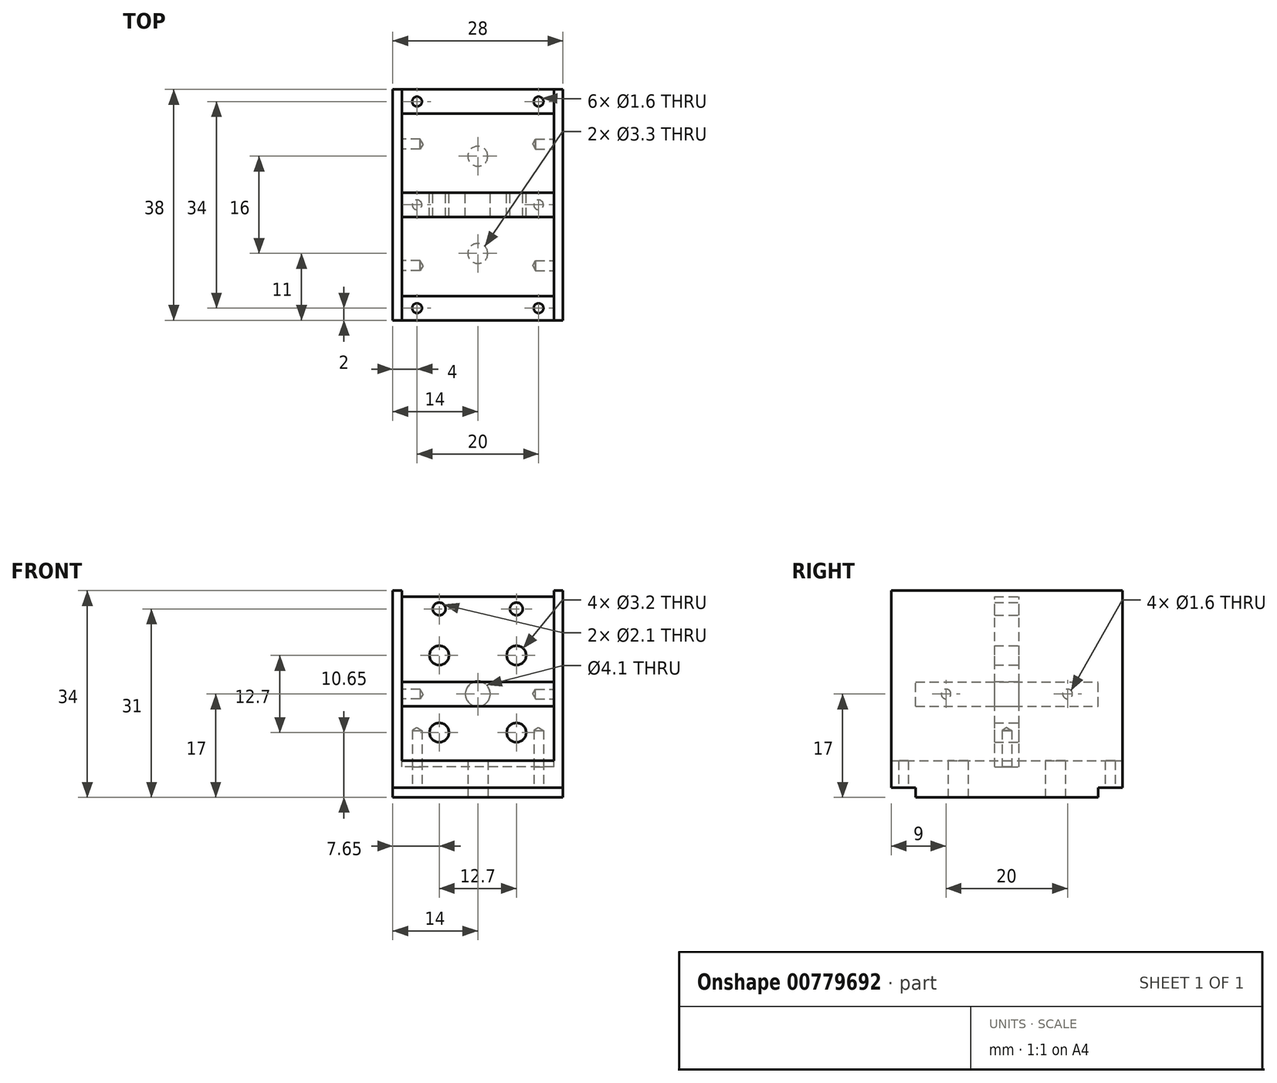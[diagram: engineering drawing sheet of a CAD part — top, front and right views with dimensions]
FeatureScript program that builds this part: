
annotation { "Feature Type Name" : "Feature", "Feature Type Description" : "" }
export const myFeature = defineFeature(function(context is Context, id is Id, definition is map)
    precondition{}
    {
        {
            var Q0;
            Q0=qCreatedBy(makeId("Front.planeOp"),FACE);
            var sketch = newSketch(context, id + "F0", { "sketchPlane" : qUnion([Q0])});
            skLineSegment(sketch, "E0.bottom", {"start": v(14, -17) * mm, "end": v(-14, -17) * mm});
            skLineSegment(sketch, "E0.top", {"start": v(14, 17) * mm, "end": v(12.5, 17) * mm});
            skLineSegment(sketch, "E0.left", {"start": v(14, -17) * mm, "end": v(14, 17) * mm});
            skLineSegment(sketch, "E0.right", {"start": v(-14, -17) * mm, "end": v(-14, 17) * mm});
            skPoint(sketch, "E0.middle", {"position": v(0, 0) * mm});
            skLineSegment(sketch, "E1.bottom", {"start": v(12.5, -11) * mm, "end": v(-12.5, -11) * mm});
            skLineSegment(sketch, "E1.left", {"start": v(12.5, -11) * mm, "end": v(12.5, 17) * mm});
            skLineSegment(sketch, "E1.right", {"start": v(-12.5, -11) * mm, "end": v(-12.5, 17) * mm});
            skLineSegment(sketch, "E2.trimOffspring", {"start": v(-12.5, 17) * mm, "end": v(-14, 17) * mm});
            skSolve(sketch);
        }
        {
            var Q0;
            Q0=makeQuery(id+"F0.imprint","IMPRINT",FACE,{"disambiguationData":[TD([[makeQuery(id+"F0.imprint","IMPRINT",EDGE,{"derivedFrom":sQuery(id+"F0.wireOp",EDGE,"E0.bottom")}),-1.0]])]});
            extrude(context, id + "F1", {"entities" : qUnion([Q0]), "endBound" : BoundingType.SYMMETRIC, "depth" : 38 * mm, "offsetDistance" : 25 * mm});
        }
        {
            var Q0;
            Q0=qCreatedBy(makeId("Front.planeOp"),FACE);
            var sketch = newSketch(context, id + "F2", { "sketchPlane" : qUnion([Q0])});
            skLineSegment(sketch, "E3.bottom", {"start": v(12.5, -2) * mm, "end": v(-12.5, -2) * mm});
            skLineSegment(sketch, "E3.top", {"start": v(12.5, 2) * mm, "end": v(-12.5, 2) * mm});
            skLineSegment(sketch, "E3.left", {"start": v(12.5, -2) * mm, "end": v(12.5, 2) * mm});
            skLineSegment(sketch, "E3.right", {"start": v(-12.5, -2) * mm, "end": v(-12.5, 2) * mm});
            skPoint(sketch, "E3.middle", {"position": v(0, 0) * mm});
            skSolve(sketch);
        }
        {
            var Q0;
            Q0=qSketchRegion(id+"F2",true);
            extrude(context, id + "F3", {"entities" : qUnion([Q0]), "endBound" : BoundingType.SYMMETRIC, "depth" : 30 * mm, "offsetDistance" : 25 * mm});
        }
        {
            var Q0;
            Q0=qCreatedBy(makeId("Front.planeOp"),FACE);
            var sketch = newSketch(context, id + "F4", { "sketchPlane" : qUnion([Q0])});
            skLineSegment(sketch, "E4.bottom", {"start": v(12.5, -12) * mm, "end": v(-12.5, -12) * mm});
            skLineSegment(sketch, "E4.top", {"start": v(12.5, 16) * mm, "end": v(-12.5, 16) * mm});
            skLineSegment(sketch, "E4.left", {"start": v(12.5, -12) * mm, "end": v(12.5, 16) * mm});
            skLineSegment(sketch, "E4.right", {"start": v(-12.5, -12) * mm, "end": v(-12.5, 16) * mm});
            skLineSegment(sketch, "E5.bottom", {"start": v(-12.5, 16) * mm, "end": v(-3.5, 16) * mm, "construction": true});
            skLineSegment(sketch, "E5.left", {"start": v(-12.5, 16) * mm, "end": v(-12.5, 12) * mm, "construction": true});
            skLineSegment(sketch, "E6", {"start": v(-12.5, 0) * mm, "end": v(12.5, 0) * mm, "construction": true});
            skLineSegment(sketch, "E7.bottom", {"start": v(12.5, 16) * mm, "end": v(-12.5, 16) * mm, "construction": true});
            skLineSegment(sketch, "E7.top", {"start": v(12.5, 12) * mm, "end": v(-12.5, 12) * mm, "construction": true});
            skLineSegment(sketch, "E7.left", {"start": v(12.5, 16) * mm, "end": v(12.5, 12) * mm, "construction": true});
            skPoint(sketch, "E8", {"position": v(0, 14) * mm});
            skPoint(sketch, "E8.positionSnap0", {"position": v(-12.5, 14) * mm});
            skCircle(sketch, "E9", {"center": v(0, 0) * mm, "radius": 2.05 * mm});
            skLineSegment(sketch, "E10.bottom", {"start": v(8.75, -8.75) * mm, "end": v(-8.75, -8.75) * mm, "construction": true});
            skLineSegment(sketch, "E10.top", {"start": v(8.75, 8.75) * mm, "end": v(-8.75, 8.75) * mm, "construction": true});
            skLineSegment(sketch, "E10.left", {"start": v(8.75, -8.75) * mm, "end": v(8.75, 8.75) * mm, "construction": true});
            skLineSegment(sketch, "E10.right", {"start": v(-8.75, -8.75) * mm, "end": v(-8.75, 8.75) * mm, "construction": true});
            skCircle(sketch, "E11", {"center": v(-6.35, 6.35) * mm, "radius": 1.6 * mm});
            skCircle(sketch, "E12", {"center": v(6.35, 6.35) * mm, "radius": 1.6 * mm});
            skCircle(sketch, "E13", {"center": v(-6.35, -6.35) * mm, "radius": 1.6 * mm});
            skCircle(sketch, "E14", {"center": v(6.35, -6.35) * mm, "radius": 1.6 * mm});
            skPoint(sketch, "E15", {"position": v(-6.35, 14) * mm});
            skPoint(sketch, "E16", {"position": v(6.35, 14) * mm});
            skCircle(sketch, "E17", {"center": v(6.35, 14) * mm, "radius": 1.05 * mm});
            skCircle(sketch, "E18", {"center": v(-6.35, 14) * mm, "radius": 1.05 * mm});
            skSolve(sketch);
        }
        {
            var Q0;
            Q0=makeQuery(id+"F4.imprint","IMPRINT",FACE,{"disambiguationData":[TD([[makeQuery(id+"F4.imprint","IMPRINT",EDGE,{"derivedFrom":sQuery(id+"F4.wireOp",EDGE,"E4.bottom")}),-1.0]])]});
            extrude(context, id + "F5", {"entities" : qUnion([Q0]), "endBound" : BoundingType.SYMMETRIC, "depth" : 4 * mm, "offsetDistance" : 25 * mm});
        }
        {
            var Q0;
            Q0=makeQuery(id+"F5.opExtrude","SWEPT_FACE",FACE,{"disambiguationData":[OSD([sQuery(id+"F4.wireOp",EDGE,"E4.bottom")])]});
            var sketch = newSketch(context, id + "F6", { "sketchPlane" : qUnion([Q0])});
            skLineSegment(sketch, "E19", {"start": v(-1, 2) * mm, "end": v(-1, -2) * mm, "construction": true});
            skPoint(sketch, "E20", {"position": v(-10, 0) * mm});
            skPoint(sketch, "E20.positionSnap0", {"position": v(-12.5, 0) * mm});
            skPoint(sketch, "E21.positionSnap0", {"position": v(12.5, 0) * mm});
            skCircle(sketch, "E22", {"center": v(-10, 0) * mm, "radius": 0.8 * mm});
            skCircle(sketch, "E23.MirrorC", {"center": v(10, 0) * mm, "radius": 0.8 * mm});
            skSolve(sketch);
        }
        {
            var Q0;
            Q0=sQuery(id+"F6.wireOp",VERTEX,"E20");
            var Q1;
            Q1=sQuery(id+"F6.wireOp",VERTEX,"E23.MirrorC.center");
            var Q2;
            Q2=makeQuery(id+"F5.opExtrude","SWEPT_BODY",BODY,{"disambiguationData":[OSD([sQuery(id+"F4.wireOp",EDGE,"E4.bottom"),sQuery(id+"F4.wireOp",EDGE,"E4.top"),sQuery(id+"F4.wireOp",EDGE,"E4.left"),sQuery(id+"F4.wireOp",EDGE,"E4.right"),sQuery(id+"F4.wireOp",EDGE,"G08tjRwT-6agX-gV4G-63M4-Xatvcd7JGdDr"),sQuery(id+"F4.wireOp",EDGE,"CjYme90i-L6Rr-A1Ub-BPvJ-hY70PV5blaYn"),sQuery(id+"F4.wireOp",EDGE,"LaCKcJXS-4cNt-ilr5-fSyq-86Lkh4RA2zMT")])]});
            hole(context, id + "F7", {"style" : HoleStyle.SIMPLE, "endStyle" : HoleEndStyle.BLIND, "holeDiameter" : 1.6 * mm, "majorDiameter" : 5 * mm, "holeDepth" : 6 * mm, "isTappedThrough" : true, "tappedDepth" : 3.9 * mm, "tapClearance" : 3, "locations" : qUnion([Q0, Q1]), "scope" : qUnion([Q2])});
        }
        {
            var Q0;
            Q0=makeQuery(id+"F1.opExtrude","SWEPT_FACE",FACE,{"disambiguationData":[OSD([sQuery(id+"F0.wireOp",EDGE,"E0.bottom")])]});
            var sketch = newSketch(context, id + "F8", { "sketchPlane" : qUnion([Q0])});
            skLineSegment(sketch, "E24.bottom", {"start": v(-14, -19) * mm, "end": v(14, -19) * mm});
            skLineSegment(sketch, "E24.top", {"start": v(-14, -15) * mm, "end": v(14, -15) * mm});
            skLineSegment(sketch, "E24.left", {"start": v(-14, -19) * mm, "end": v(-14, -15) * mm});
            skLineSegment(sketch, "E24.right", {"start": v(14, -19) * mm, "end": v(14, -15) * mm});
            skPoint(sketch, "E25", {"position": v(-10, -17) * mm});
            skPoint(sketch, "E25.positionSnap0", {"position": v(-14, -17) * mm});
            skCircle(sketch, "E26", {"center": v(-10, -17) * mm, "radius": 1.75 * mm, "construction": true});
            skCircle(sketch, "E27.MirrorC", {"center": v(10, -17) * mm, "radius": 1.75 * mm, "construction": true});
            skCircle(sketch, "E28.MirrorC", {"center": v(-10, 17) * mm, "radius": 1.75 * mm, "construction": true});
            skCircle(sketch, "E29.MirrorC", {"center": v(10, 17) * mm, "radius": 1.75 * mm, "construction": true});
            skLineSegment(sketch, "E30.MirrorCS", {"start": v(-14, 15) * mm, "end": v(14, 15) * mm});
            skPoint(sketch, "E31", {"position": v(0, -8) * mm});
            skPoint(sketch, "E32.MirrorP", {"position": v(0, 8) * mm});
            skSolve(sketch);
        }
        {
            var Q0;
            Q0=makeQuery(id+"F8.imprint","IMPRINT",FACE,{"disambiguationData":[TD([[makeQuery(id+"F8.imprint","IMPRINT",EDGE,{"derivedFrom":sQuery(id+"F8.wireOp",EDGE,"E24.bottom")}),-1.0]])]});
            var Q1;
            {var subQ0=sQuery(id+"F8.wireOp",EDGE,"E30.MirrorCS");Q1=makeQuery(id+"F8.imprint","IMPRINT",FACE,{"disambiguationData":[TD([[makeQuery(id+"F8.imprint","IMPRINT",EDGE,{"derivedFrom":subQ0}),1.0]])]});}
            extrude(context, id + "F9", {"entities" : qUnion([Q0, Q1]), "operationType" : NewBodyOperationType.REMOVE, "oppositeDirection" : true, "depth" : 1.6 * mm, "offsetDistance" : 25 * mm});
        }
        {
            var Q0;
            Q0=sQuery(id+"F8.wireOp",VERTEX,"E25");
            var Q1;
            Q1=sQuery(id+"F8.wireOp",VERTEX,"E27.MirrorC.center");
            var Q2;
            Q2=sQuery(id+"F8.wireOp",VERTEX,"E28.MirrorC.center");
            var Q3;
            Q3=sQuery(id+"F8.wireOp",VERTEX,"E29.MirrorC.center");
            var Q4;
            Q4=makeQuery(id+"F1.opExtrude","SWEPT_BODY",BODY,{"disambiguationData":[OSD([sQuery(id+"F0.wireOp",EDGE,"E0.bottom"),sQuery(id+"F0.wireOp",EDGE,"E0.top"),sQuery(id+"F0.wireOp",EDGE,"E0.left"),sQuery(id+"F0.wireOp",EDGE,"E0.right"),sQuery(id+"F0.wireOp",EDGE,"E1.bottom"),sQuery(id+"F0.wireOp",EDGE,"E1.left"),sQuery(id+"F0.wireOp",EDGE,"E1.right"),sQuery(id+"F0.wireOp",EDGE,"E2.trimOffspring")])]});
            hole(context, id + "F10", {"style" : HoleStyle.SIMPLE, "endStyle" : HoleEndStyle.BLIND, "holeDiameter" : 1.6 * mm, "majorDiameter" : 5 * mm, "holeDepth" : 6 * mm, "isTappedThrough" : true, "tappedDepth" : 3.9 * mm, "tapClearance" : 3, "locations" : qUnion([Q0, Q1, Q2, Q3]), "scope" : qUnion([Q4])});
        }
        {
            var Q0;
            Q0=sQuery(id+"F8.wireOp",VERTEX,"E31");
            var Q1;
            Q1=sQuery(id+"F8.wireOp",VERTEX,"E32.MirrorP");
            var Q2;
            Q2=makeQuery(id+"F1.opExtrude","SWEPT_BODY",BODY,{"disambiguationData":[OSD([sQuery(id+"F0.wireOp",EDGE,"E0.bottom"),sQuery(id+"F0.wireOp",EDGE,"E0.top"),sQuery(id+"F0.wireOp",EDGE,"E0.left"),sQuery(id+"F0.wireOp",EDGE,"E0.right"),sQuery(id+"F0.wireOp",EDGE,"E1.bottom"),sQuery(id+"F0.wireOp",EDGE,"E1.left"),sQuery(id+"F0.wireOp",EDGE,"E1.right"),sQuery(id+"F0.wireOp",EDGE,"E2.trimOffspring")])]});
            hole(context, id + "F11", {"style" : HoleStyle.SIMPLE, "endStyle" : HoleEndStyle.BLIND, "standardTappedOrClearance" : lookupTablePath({ "standard" : "ISO", "engagement" : "75%", "pitch" : "0.7 mm", "size" : "M4", "type" : "Tapped" }), "standardBlindInLast" : lookupTablePath({ "standard" : "ISO", "engagement" : "75%", "pitch" : "0.7 mm", "size" : "M4", "type" : "Tapped" }), "holeDiameter" : 3.3 * mm, "majorDiameter" : 4 * mm, "showTappedDepth" : true, "holeDepth" : 6 * mm, "isTappedThrough" : true, "tappedDepth" : 3.9 * mm, "tapClearance" : 3, "locations" : qUnion([Q0, Q1]), "scope" : qUnion([Q2])});
        }
        {
            var Q0;
            Q0=makeQuery(id+"F3.opExtrude","SWEPT_FACE",FACE,{"disambiguationData":[OSD([sQuery(id+"F2.wireOp",EDGE,"E3.right")])]});
            var sketch = newSketch(context, id + "F12", { "sketchPlane" : qUnion([Q0])});
            skPoint(sketch, "E33", {"position": v(-10, 0) * mm});
            skPoint(sketch, "E33.positionSnap0", {"position": v(-15, 0) * mm});
            skPoint(sketch, "E34.MirrorP", {"position": v(10, 0) * mm});
            skSolve(sketch);
        }
        {
            var Q0;
            Q0=makeQuery(id+"F3.opExtrude","SWEPT_FACE",FACE,{"disambiguationData":[OSD([sQuery(id+"F2.wireOp",EDGE,"E3.left")])]});
            var sketch = newSketch(context, id + "F13", { "sketchPlane" : qUnion([Q0])});
            skPoint(sketch, "E35", {"position": v(-10, 0) * mm});
            skPoint(sketch, "E36.MirrorP", {"position": v(10, 0) * mm});
            skSolve(sketch);
        }
        {
            var Q0;
            Q0=sQuery(id+"F13.wireOp",VERTEX,"E35");
            var Q1;
            Q1=sQuery(id+"F13.wireOp",VERTEX,"E36.MirrorP");
            var Q2;
            Q2=sQuery(id+"F12.wireOp",VERTEX,"E33");
            var Q3;
            Q3=sQuery(id+"F12.wireOp",VERTEX,"E34.MirrorP");
            var Q4;
            Q4=makeQuery(id+"F3.opExtrude","SWEPT_BODY",BODY,{"disambiguationData":[OSD([sQuery(id+"F2.wireOp",EDGE,"E3.bottom"),sQuery(id+"F2.wireOp",EDGE,"E3.top"),sQuery(id+"F2.wireOp",EDGE,"E3.left"),sQuery(id+"F2.wireOp",EDGE,"E3.right")])]});
            hole(context, id + "F14", {"style" : HoleStyle.SIMPLE, "endStyle" : HoleEndStyle.BLIND, "holeDiameter" : 1.6 * mm, "majorDiameter" : 5 * mm, "holeDepth" : 3 * mm, "isTappedThrough" : true, "tappedDepth" : 3.9 * mm, "tapClearance" : 3, "locations" : qUnion([Q0, Q1, Q2, Q3]), "scope" : qUnion([Q4])});
        }
    });
